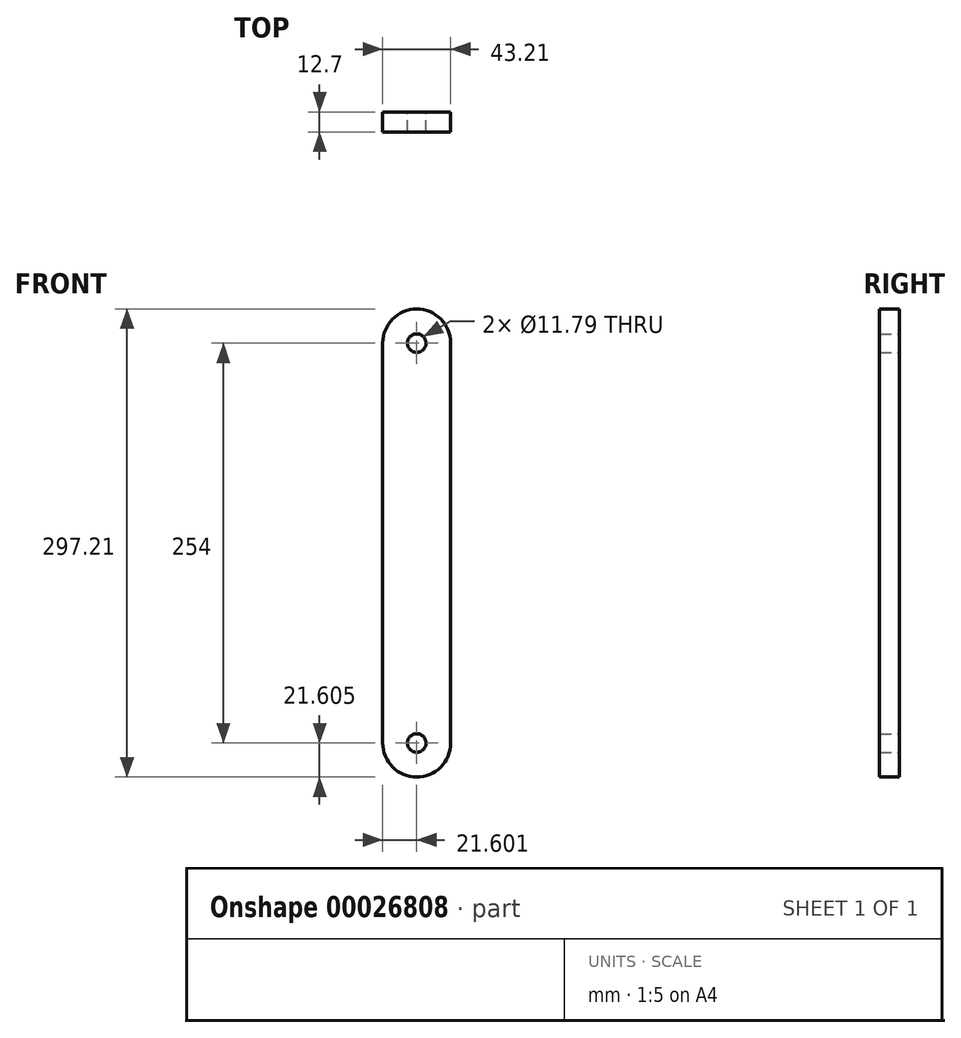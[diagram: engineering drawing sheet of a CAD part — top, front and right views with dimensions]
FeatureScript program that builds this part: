
annotation { "Feature Type Name" : "Feature", "Feature Type Description" : "" }
export const myFeature = defineFeature(function(context is Context, id is Id, definition is map)
    precondition{}
    {
        {
            var Q0;
            Q0=qCreatedBy(makeId("Front.planeOp"),FACE);
            var sketch = newSketch(context, id + "F0", { "sketchPlane" : qUnion([Q0])});
            skLineSegment(sketch, "E0.bottom", {"start": v(-23.24, 210.34) * mm, "end": v(19.97, 210.34) * mm});
            skLineSegment(sketch, "E0.top", {"start": v(-23.24, -43.66) * mm, "end": v(19.97, -43.66) * mm});
            skLineSegment(sketch, "E0.left", {"start": v(-23.24, 210.34) * mm, "end": v(-23.24, -43.66) * mm});
            skLineSegment(sketch, "E0.right", {"start": v(19.97, 210.34) * mm, "end": v(19.97, -43.66) * mm});
            skArc(sketch, "E1", {"start": v(19.97, 210.34) * mm, "mid": v(-1.64, 231.95) * mm, "end": v(-23.24, 210.34) * mm});
            skCircle(sketch, "E2", {"center": v(-1.64, 210.34) * mm, "radius": 5.9 * mm});
            skArc(sketch, "E3", {"start": v(-23.24, -43.66) * mm, "mid": v(-1.64, -65.26) * mm, "end": v(19.97, -43.66) * mm});
            skCircle(sketch, "E4", {"center": v(-1.64, -43.66) * mm, "radius": 5.9 * mm});
            skSolve(sketch);
        }
        {
            var Q0;
            Q0=makeQuery(id+"F0.imprint","IMPRINT",FACE,{"disambiguationData":[TD([[makeQuery(id+"F0.imprint","IMPRINT",EDGE,{"derivedFrom":sQuery(id+"F0.wireOp",EDGE,"E0.top")}),1.0]])]});
            var Q1;
            {var subQ0=sQuery(id+"F0.wireOp",EDGE,"E1");Q1=makeQuery(id+"F0.imprint","IMPRINT",FACE,{"disambiguationData":[TD([[makeQuery(id+"F0.imprint","IMPRINT",EDGE,{"derivedFrom":subQ0}),1.0]])]});}
            extrude(context, id + "F1", {"entities" : qUnion([Q0, Q1]), "depth" : 6.35 * mm});
        }
        {
            var Q0;
            Q0 = qSketchRegion(id + "F0", true);
            extrude(context, id + "F2", {"entities" : qUnion([Q0]), "operationType" : NewBodyOperationType.ADD, "depth" : 12.7 * mm});
        }
    });
